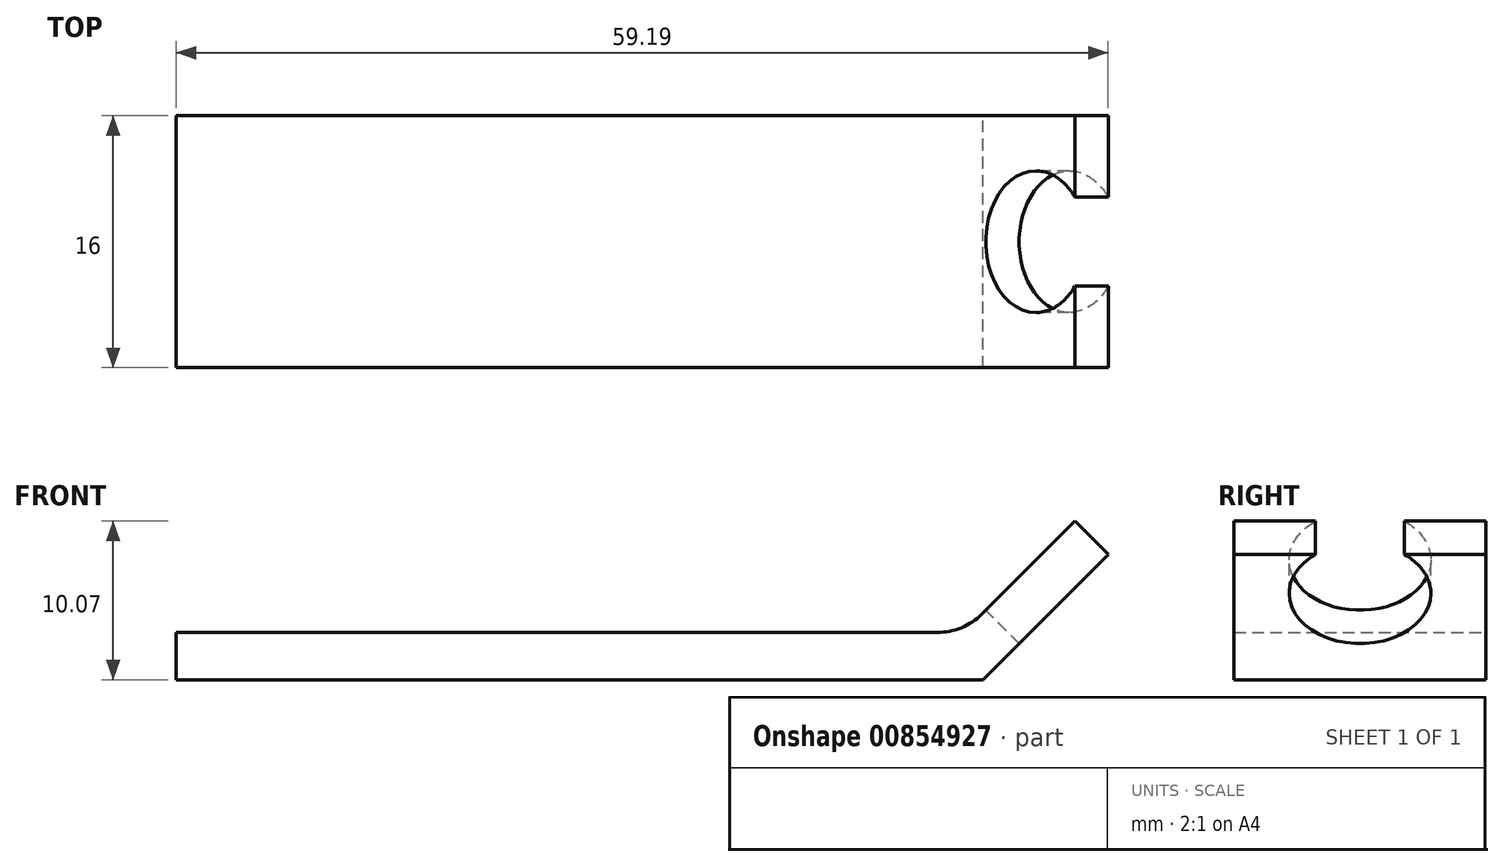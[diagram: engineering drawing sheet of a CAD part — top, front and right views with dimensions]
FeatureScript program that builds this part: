
annotation { "Feature Type Name" : "Feature", "Feature Type Description" : "" }
export const myFeature = defineFeature(function(context is Context, id is Id, definition is map)
    precondition{}
    {
        {
            var Q0;
            Q0=qCreatedBy(makeId("Front.planeOp"),FACE);
            var sketch = newSketch(context, id + "F0", { "sketchPlane" : qUnion([Q0])});
            skLineSegment(sketch, "E0", {"start": v(0, 0) * mm, "end": v(-50, 0) * mm});
            skLineSegment(sketch, "E1", {"start": v(-50, 0) * mm, "end": v(-50, -3) * mm});
            skLineSegment(sketch, "E2", {"start": v(0, 0) * mm, "end": v(9.2, 9.2) * mm});
            skLineSegment(sketch, "E3", {"start": v(11.31, 7.07) * mm, "end": v(9.2, 9.2) * mm});
            skLineSegment(sketch, "E4", {"start": v(-50, -3) * mm, "end": v(1.24, -3) * mm});
            skLineSegment(sketch, "E5", {"start": v(11.31, 7.07) * mm, "end": v(1.24, -3) * mm});
            skSolve(sketch);
        }
        {
            var Q0;
            Q0=makeQuery(id+"F0.imprint","IMPRINT",FACE,{"disambiguationData":[TD([[makeQuery(id+"F0.imprint","IMPRINT",EDGE,{"derivedFrom":sQuery(id+"F0.wireOp",EDGE,"E0")}),1.0]])]});
            extrude(context, id + "F1", {"entities" : qUnion([Q0]), "depth" : 16 * mm, "offsetDistance" : 25 * mm});
        }
        {
            var Q0;
            Q0=makeQuery(id+"F1.opExtrude","SWEPT_FACE",FACE,{"disambiguationData":[OSD([sQuery(id+"F0.wireOp",EDGE,"E2")])]});
            var sketch = newSketch(context, id + "F2", { "sketchPlane" : qUnion([Q0])});
            skLineSegment(sketch, "E6", {"start": v(16, 13) * mm, "end": v(0, 0) * mm, "construction": true});
            skLineSegment(sketch, "E7", {"start": v(0, 13) * mm, "end": v(16, 0) * mm, "construction": true});
            skCircle(sketch, "E8", {"center": v(8, 6.5) * mm, "radius": 4.5 * mm});
            skLineSegment(sketch, "E9", {"start": v(0, 10) * mm, "end": v(16, 10) * mm});
            skSolve(sketch);
        }
        {
            var Q0;
            Q0=makeQuery(id+"F2.imprint","IMPRINT",FACE,{"disambiguationData":[TD([[makeQuery(id+"F2.imprint","IMPRINT",EDGE,{"derivedFrom":sQuery(id+"F2.wireOp",EDGE,"E8")}),1.0]])]});
            var Q1;
            {var subQ0=sQuery(id+"F0.wireOp",EDGE,"E2");var subQ1=makeQuery(id+"F1.opExtrude","SWEPT_EDGE",EDGE,{"disambiguationData":[OSD([subQ0,sQuery(id+"F0.wireOp",EDGE,"E3")])]});Q1=makeQuery(id+"F2.imprint","IMPRINT",FACE,{"disambiguationData":[TD([[makeQuery(id+"F2.imprint","IMPRINT",EDGE,{"derivedFrom":subQ1}),1.0]])]});}
            extrude(context, id + "F3", {"entities" : qUnion([Q0, Q1]), "operationType" : NewBodyOperationType.REMOVE, "oppositeDirection" : true, "depth" : 25 * mm, "offsetDistance" : 25 * mm});
        }
        {
            var Q0;
            Q0=makeQuery(id+"F1.opExtrude","SWEPT_EDGE",EDGE,{"disambiguationData":[OSD([sQuery(id+"F0.wireOp",EDGE,"E0"),sQuery(id+"F0.wireOp",EDGE,"E2")])]});
            fillet(context, id + "F4", {"entities" : qUnion([Q0]), "radius" : 4 * mm, "tangentPropagation" : true, "allowEdgeOverflow" : false});
        }
    });
